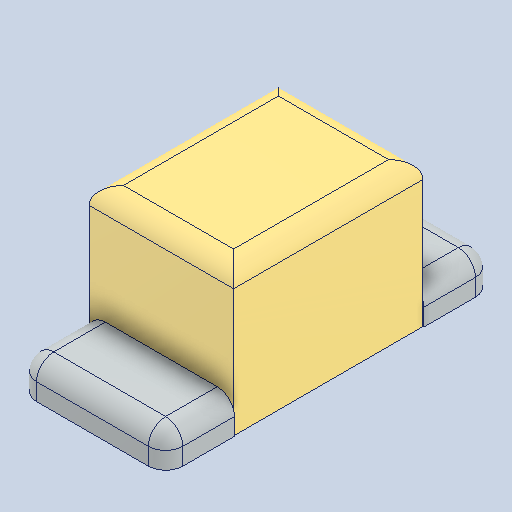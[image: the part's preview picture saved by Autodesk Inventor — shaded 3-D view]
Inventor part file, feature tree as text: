
AUTODESK INVENTOR PART (.ipt)
format: ipt  version: 2024 (Build 280153000, 153)  size: 136,704 bytes
history: native  units: in
note: dims shown in document units (in); Inventor stores cm internally (conversion verified against a paired STEP export)
features: fillet x1
ambient origin geometry x8: Origin, YZ Plane, XZ Plane, XY Plane, X Axis, Y Axis, Z Axis, Center Point
bodies: Solid1 (feature_tree)
feature tree (1):
  fillet  "Fillet3"  [1 undecoded]
note: 1 required parameter value undecoded (feature->parameter linkage not recoverable at this tier; creation-order binding heuristic only, values carry confidence <= 0.55)
